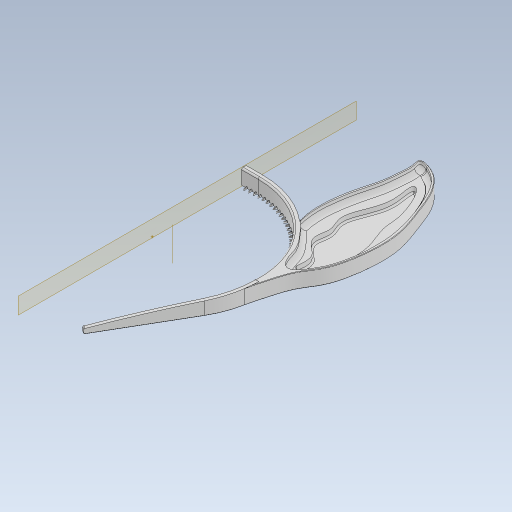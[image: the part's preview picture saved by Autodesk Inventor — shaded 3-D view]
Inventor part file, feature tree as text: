
AUTODESK INVENTOR PART (.ipt)
format: ipt  version: 2023 (Build 270158030, 158C)  size: 1,410,048 bytes
history: native  units: in
note: dims shown in document units (in); Inventor stores cm internally (conversion verified against a paired STEP export)
features: fillet x19, extrude x11, sketch x10, projected_geometry x5, chamfer x2, other x1, pattern_circular x1, mirror x1
ambient origin geometry x8: Origin, YZ Plane, XZ Plane, XY Plane, X Axis, Y Axis, Z Axis, Center Point
bodies: Solid1 (feature_tree), Solid2 (feature_tree)
feature tree (50):
  extrude  "Extrusion1"  Depth=0.1181in
  extrude  "Extrusion2"  Depth=0.3937in TaperAngle=0.0deg
  fillet  "Fillet2"  Radius=0.0433in
  other  "Work Axis1"
  pattern_circular  "Circular Pattern1"  Count=30  [1 undecoded]
  extrude  "Extrusion4"  Depth=4.3307in
  fillet  "Fillet6"  Radius=25.1969in
  fillet  "Fillet7"  Radius=0.7087in
  fillet  "Fillet8"  Radius=4.3307in
  extrude  "Extrusion10"  TaperAngle=0.0deg  [1 undecoded]
  extrude  "Extrusion11"  Depth=0.0394in
  extrude  "Extrusion12"  Depth=0.3937in TaperAngle=0.0deg
  fillet  "Fillet32"  Radius=0.315in
  fillet  "Fillet33"  Radius=0.0591in
  fillet  "Fillet35"  Radius=0.0591in
  chamfer  "Chamfer2"  Distance=0.3346in
  fillet  "Fillet36"  Radius=2.3495in
  mirror  "Mirror1"
  fillet  "Fillet30"  Radius=2.2052in
  fillet  "Fillet28"  Radius=2.0826in
  fillet  "Fillet19"  Radius=1.4138in
  extrude  "Extrusion5"  Depth=1.4901in
  extrude  "Extrusion7"  Depth=2.1896in
  extrude  "Extrusion6"  Depth=2.5146in
  fillet  "Fillet20"  Radius=2.7368in
  fillet  "Fillet21"  Radius=1.4623in
  fillet  "Fillet22"  Radius=0.488in
  fillet  "Fillet23"  Radius=0.3104in
  fillet  "Fillet24"  Radius=0.2859in
  fillet  "Fillet25"  Radius=0.2088in
  fillet  "Fillet26"  Radius=0.2171in
  extrude  "Extrusion8"  Depth=0.23in
  fillet  "Fillet27"  Radius=0.2362in
  extrude  "Extrusion9"  Depth=0.0787in
  chamfer  "Chamfer1"  Distance=0.0787in
  sketch  "Sketch1"  dims[d23=2.2638in d25=0.1181in]
  sketch  "Sketch2"  dims[d27=0.1181in d30=0.3937in d31=0.0in d48=0.0433in d49=0.0in]
  sketch  "Sketch7"  dims[d50=0.0118in]
  sketch  "Sketch8"  dims[d57=0.0787in d58=0.0157in d61=11.811in d62=-0.6184in]
  sketch  "Sketch9"  dims[d65=3.1496in d76=4.3307in d77=25.1969in d78=0.7087in d79=4.3307in]
  sketch  "Sketch11"  dims[d80=0.3937in d81=0.0in d82=0.0in]
  sketch  "Sketch12"  dims[d86=0.0394in d87=0.0394in]
  projected_geometry  "Projected Loop1"
  sketch  "Sketch13"  dims[d88=0.0236in d104=0.3937in d105=0.0in d107=0.315in d108=0.0in d121=0.0591in d122=0.0591in]
  projected_geometry  "Projected Loop2"
  projected_geometry  "Projected Loop3"
  sketch  "Sketch14"  dims[d123=1.378in d125=0.3346in d126=0.0in d130=2.3495in d131=2.2052in d132=2.0826in d133=1.4138in]
  projected_geometry  "Projected Loop4"
  sketch  "Sketch16"  dims[d134=2.5284in d135=1.4901in d136=2.1896in d137=2.5146in d138=2.7368in d139=1.4623in d140=0.488in d141=0.3104in d142=0.2859in d143=0.2088in d144=0.2171in d145=0.23in d147=0.2362in d148=0.0787in d149=0.0787in d150=0.0394in d153=0.0394in d154=0.1181in d155=0.0787in d156=0.0787in d158=23.622in d159=1.9685in d161=7.8078in d162=2.3622in d163=0.7874in d164=0.9817in d165=0.0in d167=0.0787in d168=0.1969in d169=0.1969in d170=0.1181in d171=0.0197in d172=0.0079in d173=0.0394in d174=0.0197in d175=0.0197in d182=0.0984in d183=0.0394in d184=0.0984in d185=0.0394in d186=0.0591in d187=0.0394in d188=0.0197in d189=0.076in d190=0.0in d191=0.0in d192=0.0079in d193=0.0197in d194=0.0787in d195=45.0deg d196=0.0in d197=0.0in d199=0.3937in d200=0.0in d201=0.3543in d202=0.0in d203=0.315in d205=0.1969in d206=0.0in d207=0.1181in d209=0.0118in d210=0.1181in d212=0.0394in d213=0.015in d214=0.0787in d215=45.0deg d216=0.7874in d217=0.4331in d218=2.3622in d219=0.4331in d220=0.0984in d221=0.3937in d222=0.1181in d223=0.2362in]
  projected_geometry  "Projected Loop5"
note: 2 required parameter values undecoded (feature->parameter linkage not recoverable at this tier; creation-order binding heuristic only, values carry confidence <= 0.55)
